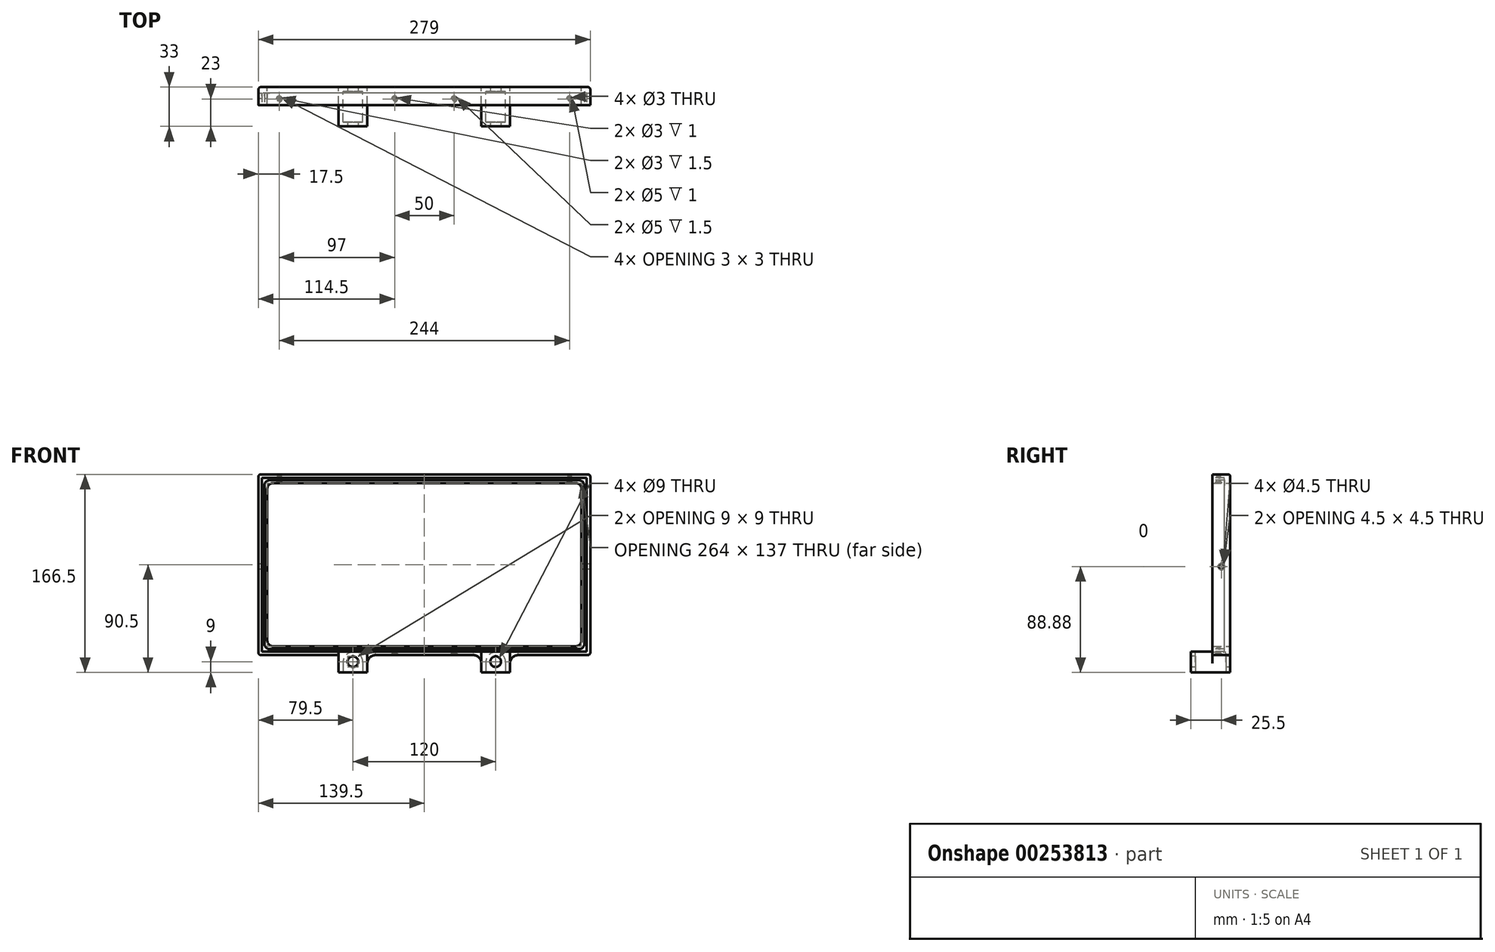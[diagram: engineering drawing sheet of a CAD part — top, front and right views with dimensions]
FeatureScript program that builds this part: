
annotation { "Feature Type Name" : "Feature", "Feature Type Description" : "" }
export const myFeature = defineFeature(function(context is Context, id is Id, definition is map)
    precondition{}
    {
        {
            var Q0;
            Q0=qCreatedBy(makeId("Front.planeOp"),FACE);
            var sketch = newSketch(context, id + "F0", { "sketchPlane" : qUnion([Q0])});
            skLineSegment(sketch, "E0.bottom", {"start": v(132, -68.5) * mm, "end": v(-132, -68.5) * mm});
            skLineSegment(sketch, "E0.top", {"start": v(132, 68.5) * mm, "end": v(-132, 68.5) * mm});
            skLineSegment(sketch, "E0.left", {"start": v(132, -68.5) * mm, "end": v(132, 68.5) * mm});
            skLineSegment(sketch, "E0.right", {"start": v(-132, -68.5) * mm, "end": v(-132, 68.5) * mm});
            skPoint(sketch, "E0.middle", {"position": v(0, 0) * mm});
            skLineSegment(sketch, "E1.bottom", {"start": v(139.5, -76) * mm, "end": v(-139.5, -76) * mm});
            skLineSegment(sketch, "E1.top", {"start": v(139.5, 76) * mm, "end": v(-139.5, 76) * mm});
            skLineSegment(sketch, "E1.left", {"start": v(139.5, -76) * mm, "end": v(139.5, 76) * mm});
            skLineSegment(sketch, "E1.right", {"start": v(-139.5, -76) * mm, "end": v(-139.5, 76) * mm});
            skSolve(sketch);
        }
        {
            var Q0;
            Q0 = qSketchRegion(id + "F0", true);
            extrude(context, id + "F1", {"entities" : qUnion([Q0]), "depth" : 15 * mm});
        }
        {
            var Q0;
            Q0=makeQuery(id+"F1.opExtrude","CAP_FACE",FACE,{"disambiguationData":[OSD([sQuery(id+"F0.wireOp",EDGE,"E0.bottom"),sQuery(id+"F0.wireOp",EDGE,"E0.top"),sQuery(id+"F0.wireOp",EDGE,"E0.left"),sQuery(id+"F0.wireOp",EDGE,"E0.right"),sQuery(id+"F0.wireOp",EDGE,"E1.bottom"),sQuery(id+"F0.wireOp",EDGE,"E1.top"),sQuery(id+"F0.wireOp",EDGE,"E1.left"),sQuery(id+"F0.wireOp",EDGE,"E1.right")])],"isStart":false});
            var sketch = newSketch(context, id + "F2", { "sketchPlane" : qUnion([Q0])});
            skLineSegment(sketch, "E2.bottom", {"start": v(-72, -73) * mm, "end": v(-48, -73) * mm});
            skLineSegment(sketch, "E2.top", {"start": v(-72, -76) * mm, "end": v(-48, -76) * mm});
            skLineSegment(sketch, "E2.left", {"start": v(-72, -73) * mm, "end": v(-72, -76) * mm});
            skLineSegment(sketch, "E2.right", {"start": v(-48, -73) * mm, "end": v(-48, -76) * mm});
            skLineSegment(sketch, "E3.bottom", {"start": v(48, -73) * mm, "end": v(72, -73) * mm});
            skLineSegment(sketch, "E3.top", {"start": v(48, -76) * mm, "end": v(72, -76) * mm});
            skLineSegment(sketch, "E3.left", {"start": v(48, -73) * mm, "end": v(48, -76) * mm});
            skLineSegment(sketch, "E3.right", {"start": v(72, -73) * mm, "end": v(72, -76) * mm});
            skSolve(sketch);
        }
        {
            var Q0;
            Q0 = qSketchRegion(id + "F2", true);
            extrude(context, id + "F3", {"entities" : qUnion([Q0]), "operationType" : NewBodyOperationType.ADD, "depth" : 18 * mm, "offsetDistance" : 25 * mm});
        }
        {
            var Q0;
            Q0=makeQuery(id+"F3.boolean.opBoolean","MERGE",FACE,{"derivedFrom":[makeQuery(id+"F1.opExtrude","SWEPT_FACE",FACE,{"disambiguationData":[OSD([sQuery(id+"F0.wireOp",EDGE,"E1.bottom")])]}),makeQuery(id+"F3.opExtrude","SWEPT_FACE",FACE,{"disambiguationData":[OSD([sQuery(id+"F2.wireOp",EDGE,"E2.top")])]}),makeQuery(id+"F3.opExtrude","SWEPT_FACE",FACE,{"disambiguationData":[OSD([sQuery(id+"F2.wireOp",EDGE,"E3.top")])]})]});
            var sketch = newSketch(context, id + "F4", { "sketchPlane" : qUnion([Q0])});
            skLineSegment(sketch, "E4.bottom", {"start": v(-72, 33) * mm, "end": v(-48, 33) * mm});
            skLineSegment(sketch, "E4.top", {"start": v(-72, 0) * mm, "end": v(-48, 0) * mm});
            skLineSegment(sketch, "E4.left", {"start": v(-72, 33) * mm, "end": v(-72, 0) * mm});
            skLineSegment(sketch, "E4.right", {"start": v(-48, 33) * mm, "end": v(-48, 0) * mm});
            skLineSegment(sketch, "E5.bottom", {"start": v(48, 33) * mm, "end": v(72, 33) * mm});
            skLineSegment(sketch, "E5.top", {"start": v(48, 0) * mm, "end": v(72, 0) * mm});
            skLineSegment(sketch, "E5.left", {"start": v(48, 33) * mm, "end": v(48, 0) * mm});
            skLineSegment(sketch, "E5.right", {"start": v(72, 33) * mm, "end": v(72, 0) * mm});
            skSolve(sketch);
        }
        {
            var Q0;
            Q0 = qSketchRegion(id + "F4", true);
            extrude(context, id + "F5", {"entities" : qUnion([Q0]), "operationType" : NewBodyOperationType.ADD, "depth" : 14.5 * mm});
        }
        {
            var Q0;
            Q0=makeQuery(id+"F5.opExtrude","CAP_FACE",FACE,{"disambiguationData":[OSD([sQuery(id+"F4.wireOp",EDGE,"E4.bottom"),sQuery(id+"F4.wireOp",EDGE,"E4.top"),sQuery(id+"F4.wireOp",EDGE,"E4.left"),sQuery(id+"F4.wireOp",EDGE,"E4.right")])],"isStart":false});
            var sketch = newSketch(context, id + "F6", { "sketchPlane" : qUnion([Q0])});
            skLineSegment(sketch, "E6.bottom", {"start": v(-68.3, 29.3) * mm, "end": v(-51.7, 29.3) * mm});
            skLineSegment(sketch, "E6.top", {"start": v(-68.3, 3.7) * mm, "end": v(-51.7, 3.7) * mm});
            skLineSegment(sketch, "E6.left", {"start": v(-68.3, 29.3) * mm, "end": v(-68.3, 3.7) * mm});
            skLineSegment(sketch, "E6.right", {"start": v(-51.7, 29.3) * mm, "end": v(-51.7, 3.7) * mm});
            skSolve(sketch);
        }
        {
            var Q0;
            Q0=makeQuery(id+"F5.opExtrude","CAP_FACE",FACE,{"disambiguationData":[OSD([sQuery(id+"F4.wireOp",EDGE,"E5.bottom"),sQuery(id+"F4.wireOp",EDGE,"E5.top"),sQuery(id+"F4.wireOp",EDGE,"E5.left"),sQuery(id+"F4.wireOp",EDGE,"E5.right")])],"isStart":false});
            var sketch = newSketch(context, id + "F7", { "sketchPlane" : qUnion([Q0])});
            skLineSegment(sketch, "E7.bottom", {"start": v(51.7, 29.3) * mm, "end": v(68.3, 29.3) * mm});
            skLineSegment(sketch, "E7.top", {"start": v(51.7, 3.7) * mm, "end": v(68.3, 3.7) * mm});
            skLineSegment(sketch, "E7.left", {"start": v(51.7, 29.3) * mm, "end": v(51.7, 3.7) * mm});
            skLineSegment(sketch, "E7.right", {"start": v(68.3, 29.3) * mm, "end": v(68.3, 3.7) * mm});
            skSolve(sketch);
        }
        {
            var Q0;
            Q0 = qSketchRegion(id + "F6", true);
            var Q1;
            Q1 = qSketchRegion(id + "F7", true);
            extrude(context, id + "F8", {"entities" : qUnion([Q0, Q1]), "operationType" : NewBodyOperationType.REMOVE, "oppositeDirection" : true, "depth" : 8.7 * mm});
        }
        {
            var Q0;
            Q0=makeQuery(id+"F8.boolean.opBoolean","COPY",FACE,{"derivedFrom":makeQuery(id+"F8.opExtrude","SWEPT_FACE",FACE,{"disambiguationData":[OSD([sQuery(id+"F6.wireOp",EDGE,"E6.top")])]})});
            var sketch = newSketch(context, id + "F9", { "sketchPlane" : qUnion([Q0])});
            skCircle(sketch, "E8", {"center": v(-60, -81.8) * mm, "radius": 8.3 * mm});
            skSolve(sketch);
        }
        {
            var Q0;
            Q0=makeQuery(id+"F8.boolean.opBoolean","COPY",FACE,{"derivedFrom":makeQuery(id+"F8.opExtrude","SWEPT_FACE",FACE,{"disambiguationData":[OSD([sQuery(id+"F7.wireOp",EDGE,"E7.top")])]})});
            var sketch = newSketch(context, id + "F10", { "sketchPlane" : qUnion([Q0])});
            skCircle(sketch, "E9", {"center": v(60, -81.8) * mm, "radius": 8.3 * mm});
            skSolve(sketch);
        }
        {
            var Q0;
            Q0 = qSketchRegion(id + "F10", true);
            var Q1;
            Q1 = qSketchRegion(id + "F9", true);
            extrude(context, id + "F11", {"entities" : qUnion([Q0, Q1]), "operationType" : NewBodyOperationType.REMOVE, "depth" : 25.6 * mm});
        }
        {
            var Q0;
            Q0=makeQuery(id+"F5.boolean.opBoolean","MERGE",FACE,{"derivedFrom":[makeQuery(id+"F3.opExtrude","CAP_FACE",FACE,{"disambiguationData":[OSD([sQuery(id+"F2.wireOp",EDGE,"E2.bottom"),sQuery(id+"F2.wireOp",EDGE,"E2.top"),sQuery(id+"F2.wireOp",EDGE,"E2.left"),sQuery(id+"F2.wireOp",EDGE,"E2.right")])],"isStart":false}),makeQuery(id+"F5.opExtrude","SWEPT_FACE",FACE,{"disambiguationData":[OSD([sQuery(id+"F4.wireOp",EDGE,"E4.bottom")])]})]});
            var sketch = newSketch(context, id + "F12", { "sketchPlane" : qUnion([Q0])});
            skCircle(sketch, "E10", {"center": v(-60, -81.5) * mm, "radius": 4.5 * mm});
            skSolve(sketch);
        }
        {
            var Q0;
            Q0=makeQuery(id+"F5.boolean.opBoolean","MERGE",FACE,{"derivedFrom":[makeQuery(id+"F3.opExtrude","CAP_FACE",FACE,{"disambiguationData":[OSD([sQuery(id+"F2.wireOp",EDGE,"E3.bottom"),sQuery(id+"F2.wireOp",EDGE,"E3.top"),sQuery(id+"F2.wireOp",EDGE,"E3.left"),sQuery(id+"F2.wireOp",EDGE,"E3.right")])],"isStart":false}),makeQuery(id+"F5.opExtrude","SWEPT_FACE",FACE,{"disambiguationData":[OSD([sQuery(id+"F4.wireOp",EDGE,"E5.bottom")])]})]});
            var sketch = newSketch(context, id + "F13", { "sketchPlane" : qUnion([Q0])});
            skCircle(sketch, "E11", {"center": v(60, -81.5) * mm, "radius": 4.5 * mm});
            skSolve(sketch);
        }
        {
            var Q0;
            Q0 = qSketchRegion(id + "F13", true);
            var Q1;
            Q1 = qSketchRegion(id + "F12", true);
            extrude(context, id + "F14", {"entities" : qUnion([Q0, Q1]), "operationType" : NewBodyOperationType.REMOVE, "endBound" : BoundingType.THROUGH_ALL, "oppositeDirection" : true, "depth" : 25 * mm});
        }
        {
            var Q0;
            Q0=makeQuery(id+"F1.opExtrude","CAP_FACE",FACE,{"disambiguationData":[OSD([sQuery(id+"F0.wireOp",EDGE,"E0.bottom"),sQuery(id+"F0.wireOp",EDGE,"E0.top"),sQuery(id+"F0.wireOp",EDGE,"E0.left"),sQuery(id+"F0.wireOp",EDGE,"E0.right"),sQuery(id+"F0.wireOp",EDGE,"E1.bottom"),sQuery(id+"F0.wireOp",EDGE,"E1.top"),sQuery(id+"F0.wireOp",EDGE,"E1.left"),sQuery(id+"F0.wireOp",EDGE,"E1.right")])],"isStart":false});
            var sketch = newSketch(context, id + "F15", { "sketchPlane" : qUnion([Q0])});
            skPoint(sketch, "E12", {"position": v(0, 0) * mm});
            skLineSegment(sketch, "E13.bottom", {"start": v(134.5, -71) * mm, "end": v(-134.5, -71) * mm});
            skLineSegment(sketch, "E13.top", {"start": v(134.5, 71) * mm, "end": v(-134.5, 71) * mm});
            skLineSegment(sketch, "E13.left", {"start": v(134.5, -71) * mm, "end": v(134.5, 71) * mm});
            skLineSegment(sketch, "E13.right", {"start": v(-134.5, -71) * mm, "end": v(-134.5, 71) * mm});
            skLineSegment(sketch, "E14.bottom", {"start": v(136.5, -73) * mm, "end": v(-136.5, -73) * mm});
            skLineSegment(sketch, "E14.top", {"start": v(136.5, 73) * mm, "end": v(-136.5, 73) * mm});
            skLineSegment(sketch, "E14.left", {"start": v(136.5, -73) * mm, "end": v(136.5, 73) * mm});
            skLineSegment(sketch, "E14.right", {"start": v(-136.5, -73) * mm, "end": v(-136.5, 73) * mm});
            skSolve(sketch);
        }
        {
            var Q0;
            Q0 = qSketchRegion(id + "F15", true);
            extrude(context, id + "F16", {"entities" : qUnion([Q0]), "operationType" : NewBodyOperationType.REMOVE, "oppositeDirection" : true, "depth" : 10 * mm});
        }
        {
            var Q0;
            {var subQ3=sQuery(id+"F0.wireOp",EDGE,"E1.bottom");Q0=makeQuery(id+"F5.boolean.opBoolean","SPLIT",FACE,{"disambiguationData":[TD([makeQuery(id+"F3.opExtrude","SWEPT_FACE",FACE,{"disambiguationData":[OSD([sQuery(id+"F2.wireOp",EDGE,"E2.right")])]})])],"derivedFrom":makeQuery(id+"F3.boolean.opBoolean","MERGE",FACE,{"derivedFrom":[makeQuery(id+"F1.opExtrude","SWEPT_FACE",FACE,{"disambiguationData":[OSD([subQ3])]}),makeQuery(id+"F3.opExtrude","SWEPT_FACE",FACE,{"disambiguationData":[OSD([sQuery(id+"F2.wireOp",EDGE,"E2.top")])]}),makeQuery(id+"F3.opExtrude","SWEPT_FACE",FACE,{"disambiguationData":[OSD([sQuery(id+"F2.wireOp",EDGE,"E3.top")])]})]})});}
            var sketch = newSketch(context, id + "F17", { "sketchPlane" : qUnion([Q0])});
            skCircle(sketch, "E15", {"center": v(-25, 10) * mm, "radius": 1.5 * mm});
            skCircle(sketch, "E16", {"center": v(25, 10) * mm, "radius": 1.5 * mm});
            skSolve(sketch);
        }
        {
            var Q0;
            Q0 = qSketchRegion(id + "F17", true);
            extrude(context, id + "F18", {"entities" : qUnion([Q0]), "operationType" : NewBodyOperationType.REMOVE, "oppositeDirection" : true, "depth" : 6 * mm, "offsetDistance" : 25 * mm});
        }
        {
            var Q0;
            Q0=makeQuery(id+"F1.opExtrude","SWEPT_FACE",FACE,{"disambiguationData":[OSD([sQuery(id+"F0.wireOp",EDGE,"E0.top")])]});
            var sketch = newSketch(context, id + "F19", { "sketchPlane" : qUnion([Q0])});
            skCircle(sketch, "E17", {"center": v(-122, 10) * mm, "radius": 1.5 * mm});
            skCircle(sketch, "E18", {"center": v(122, 10) * mm, "radius": 1.5 * mm});
            skSolve(sketch);
        }
        {
            var Q0;
            Q0 = qSketchRegion(id + "F19", true);
            extrude(context, id + "F20", {"entities" : qUnion([Q0]), "operationType" : NewBodyOperationType.REMOVE, "oppositeDirection" : true, "depth" : 6 * mm, "offsetDistance" : 25 * mm});
        }
        {
            var Q0;
            Q0=makeQuery(id+"F1.opExtrude","CAP_EDGE",EDGE,{"disambiguationData":[OSD([sQuery(id+"F0.wireOp",EDGE,"E1.right")])],"isStart":true});
            var Q1;
            Q1=makeQuery(id+"F1.opExtrude","SWEPT_EDGE",EDGE,{"disambiguationData":[OSD([sQuery(id+"F0.wireOp",EDGE,"E1.top"),sQuery(id+"F0.wireOp",EDGE,"E1.right")])]});
            var Q2;
            Q2=makeQuery(id+"F1.opExtrude","CAP_EDGE",EDGE,{"disambiguationData":[OSD([sQuery(id+"F0.wireOp",EDGE,"E1.top")])],"isStart":true});
            var Q3;
            Q3=makeQuery(id+"F1.opExtrude","SWEPT_EDGE",EDGE,{"disambiguationData":[OSD([sQuery(id+"F0.wireOp",EDGE,"E1.bottom"),sQuery(id+"F0.wireOp",EDGE,"E1.right")])]});
            var Q4;
            {var subQ0=sQuery(id+"F0.wireOp",EDGE,"E1.right");var subQ1=sQuery(id+"F0.wireOp",EDGE,"E1.bottom");Q4=makeQuery(id+"F5.boolean.opBoolean","SPLIT",EDGE,{"disambiguationData":[TD([makeQuery(id+"F1.opExtrude","SWEPT_FACE",FACE,{"disambiguationData":[OSD([subQ0])]})])],"derivedFrom":makeQuery(id+"F1.opExtrude","CAP_EDGE",EDGE,{"disambiguationData":[OSD([subQ1])],"isStart":true})});}
            var Q5;
            {var subQ0=sQuery(id+"F0.wireOp",EDGE,"E1.bottom");Q5=makeQuery(id+"F5.boolean.opBoolean","SPLIT",EDGE,{"disambiguationData":[TD([makeQuery(id+"F3.opExtrude","SWEPT_FACE",FACE,{"disambiguationData":[OSD([sQuery(id+"F2.wireOp",EDGE,"E2.right")])]})])],"derivedFrom":makeQuery(id+"F1.opExtrude","CAP_EDGE",EDGE,{"disambiguationData":[OSD([subQ0])],"isStart":true})});}
            var Q6;
            {var subQ0=sQuery(id+"F0.wireOp",EDGE,"E1.left");var subQ1=sQuery(id+"F0.wireOp",EDGE,"E1.bottom");Q6=makeQuery(id+"F5.boolean.opBoolean","SPLIT",EDGE,{"disambiguationData":[TD([makeQuery(id+"F1.opExtrude","SWEPT_FACE",FACE,{"disambiguationData":[OSD([subQ0])]})])],"derivedFrom":makeQuery(id+"F1.opExtrude","CAP_EDGE",EDGE,{"disambiguationData":[OSD([subQ1])],"isStart":true})});}
            var Q7;
            Q7=makeQuery(id+"F1.opExtrude","SWEPT_EDGE",EDGE,{"disambiguationData":[OSD([sQuery(id+"F0.wireOp",EDGE,"E1.bottom"),sQuery(id+"F0.wireOp",EDGE,"E1.left")])]});
            var Q8;
            Q8=makeQuery(id+"F1.opExtrude","CAP_EDGE",EDGE,{"disambiguationData":[OSD([sQuery(id+"F0.wireOp",EDGE,"E1.left")])],"isStart":true});
            var Q9;
            Q9=makeQuery(id+"F1.opExtrude","SWEPT_EDGE",EDGE,{"disambiguationData":[OSD([sQuery(id+"F0.wireOp",EDGE,"E1.top"),sQuery(id+"F0.wireOp",EDGE,"E1.left")])]});
            fillet(context, id + "F21", {"entities" : qUnion([Q0, Q1, Q2, Q3, Q4, Q5, Q6, Q7, Q8, Q9]), "radius" : 2 * mm, "tangentPropagation" : true, "allowEdgeOverflow" : false});
        }
        {
            var Q0;
            Q0=makeQuery(id+"F1.opExtrude","SWEPT_FACE",FACE,{"disambiguationData":[OSD([sQuery(id+"F0.wireOp",EDGE,"E1.right")])]});
            var sketch = newSketch(context, id + "F22", { "sketchPlane" : qUnion([Q0])});
            skCircle(sketch, "E19", {"center": v(7.5, -1.62) * mm, "radius": 2.25 * mm});
            skSolve(sketch);
        }
        {
            var Q0;
            Q0 = qSketchRegion(id + "F22", true);
            extrude(context, id + "F23", {"entities" : qUnion([Q0]), "operationType" : NewBodyOperationType.REMOVE, "endBound" : BoundingType.THROUGH_ALL, "oppositeDirection" : true, "depth" : 25 * mm});
        }
        {
            var Q0;
            Q0=makeQuery(id+"F1.opExtrude","SWEPT_EDGE",EDGE,{"disambiguationData":[OSD([sQuery(id+"F0.wireOp",EDGE,"E0.top"),sQuery(id+"F0.wireOp",EDGE,"E0.right")])]});
            var Q1;
            Q1=makeQuery(id+"F16.boolean.opBoolean","COPY",EDGE,{"derivedFrom":makeQuery(id+"F16.opExtrude","SWEPT_EDGE",EDGE,{"disambiguationData":[OSD([sQuery(id+"F15.wireOp",EDGE,"E13.top"),sQuery(id+"F15.wireOp",EDGE,"E13.right")])]})});
            var Q2;
            Q2=makeQuery(id+"F1.opExtrude","SWEPT_EDGE",EDGE,{"disambiguationData":[OSD([sQuery(id+"F0.wireOp",EDGE,"E0.bottom"),sQuery(id+"F0.wireOp",EDGE,"E0.right")])]});
            var Q3;
            Q3=makeQuery(id+"F16.boolean.opBoolean","COPY",EDGE,{"derivedFrom":makeQuery(id+"F16.opExtrude","SWEPT_EDGE",EDGE,{"disambiguationData":[OSD([sQuery(id+"F15.wireOp",EDGE,"E13.bottom"),sQuery(id+"F15.wireOp",EDGE,"E13.right")])]})});
            var Q4;
            Q4=makeQuery(id+"F1.opExtrude","SWEPT_EDGE",EDGE,{"disambiguationData":[OSD([sQuery(id+"F0.wireOp",EDGE,"E0.top"),sQuery(id+"F0.wireOp",EDGE,"E0.left")])]});
            var Q5;
            Q5=makeQuery(id+"F16.boolean.opBoolean","COPY",EDGE,{"derivedFrom":makeQuery(id+"F16.opExtrude","SWEPT_EDGE",EDGE,{"disambiguationData":[OSD([sQuery(id+"F15.wireOp",EDGE,"E13.bottom"),sQuery(id+"F15.wireOp",EDGE,"E13.left")])]})});
            var Q6;
            Q6=makeQuery(id+"F1.opExtrude","SWEPT_EDGE",EDGE,{"disambiguationData":[OSD([sQuery(id+"F0.wireOp",EDGE,"E0.bottom"),sQuery(id+"F0.wireOp",EDGE,"E0.left")])]});
            var Q7;
            Q7=makeQuery(id+"F16.boolean.opBoolean","COPY",EDGE,{"derivedFrom":makeQuery(id+"F16.opExtrude","SWEPT_EDGE",EDGE,{"disambiguationData":[OSD([sQuery(id+"F15.wireOp",EDGE,"E13.top"),sQuery(id+"F15.wireOp",EDGE,"E13.left")])]})});
            fillet(context, id + "F24", {"entities" : qUnion([Q0, Q1, Q2, Q3, Q4, Q5, Q6, Q7]), "radius" : 4.5 * mm, "tangentPropagation" : true, "allowEdgeOverflow" : false});
        }
        {
            var Q0;
            Q0=makeQuery(id+"F5.opExtrude","CAP_EDGE",EDGE,{"disambiguationData":[OSD([sQuery(id+"F4.wireOp",EDGE,"E4.left")])],"isStart":true});
            var Q1;
            Q1=makeQuery(id+"F5.opExtrude","CAP_EDGE",EDGE,{"disambiguationData":[OSD([sQuery(id+"F4.wireOp",EDGE,"E5.left")])],"isStart":true});
            var Q2;
            Q2=makeQuery(id+"F5.opExtrude","CAP_EDGE",EDGE,{"disambiguationData":[OSD([sQuery(id+"F4.wireOp",EDGE,"E5.right")])],"isStart":true});
            var Q3;
            Q3=makeQuery(id+"F5.opExtrude","CAP_EDGE",EDGE,{"disambiguationData":[OSD([sQuery(id+"F4.wireOp",EDGE,"E4.right")])],"isStart":true});
            fillet(context, id + "F25", {"entities" : qUnion([Q0, Q1, Q2, Q3]), "radius" : 7 * mm, "tangentPropagation" : true, "allowEdgeOverflow" : false});
        }
        {
            var Q0;
            Q0=makeQuery(id+"F1.opExtrude","SWEPT_FACE",FACE,{"disambiguationData":[OSD([sQuery(id+"F0.wireOp",EDGE,"E0.top")])]});
            var sketch = newSketch(context, id + "F26", { "sketchPlane" : qUnion([Q0])});
            skCircle(sketch, "E20", {"center": v(-122, 10) * mm, "radius": 2.5 * mm});
            skCircle(sketch, "E21", {"center": v(122, 10) * mm, "radius": 2.5 * mm});
            skSolve(sketch);
        }
        {
            var Q0;
            Q0 = qSketchRegion(id + "F26", true);
            extrude(context, id + "F27", {"entities" : qUnion([Q0]), "operationType" : NewBodyOperationType.REMOVE, "oppositeDirection" : true, "depth" : 1 * mm, "offsetDistance" : 25 * mm});
        }
        {
            var Q0;
            {var subQ3=sQuery(id+"F0.wireOp",EDGE,"E1.bottom");Q0=makeQuery(id+"F5.boolean.opBoolean","SPLIT",FACE,{"disambiguationData":[TD([makeQuery(id+"F3.opExtrude","SWEPT_FACE",FACE,{"disambiguationData":[OSD([sQuery(id+"F2.wireOp",EDGE,"E2.right")])]})])],"derivedFrom":makeQuery(id+"F3.boolean.opBoolean","MERGE",FACE,{"derivedFrom":[makeQuery(id+"F1.opExtrude","SWEPT_FACE",FACE,{"disambiguationData":[OSD([subQ3])]}),makeQuery(id+"F3.opExtrude","SWEPT_FACE",FACE,{"disambiguationData":[OSD([sQuery(id+"F2.wireOp",EDGE,"E2.top")])]}),makeQuery(id+"F3.opExtrude","SWEPT_FACE",FACE,{"disambiguationData":[OSD([sQuery(id+"F2.wireOp",EDGE,"E3.top")])]})]})});}
            var sketch = newSketch(context, id + "F28", { "sketchPlane" : qUnion([Q0])});
            skCircle(sketch, "E22", {"center": v(-25, 10) * mm, "radius": 2.5 * mm});
            skCircle(sketch, "E23", {"center": v(25, 10) * mm, "radius": 2.5 * mm});
            skSolve(sketch);
        }
        {
            var Q0;
            Q0 = qSketchRegion(id + "F28", true);
            extrude(context, id + "F29", {"entities" : qUnion([Q0]), "operationType" : NewBodyOperationType.REMOVE, "oppositeDirection" : true, "depth" : 1.5 * mm, "offsetDistance" : 25 * mm});
        }
    });
